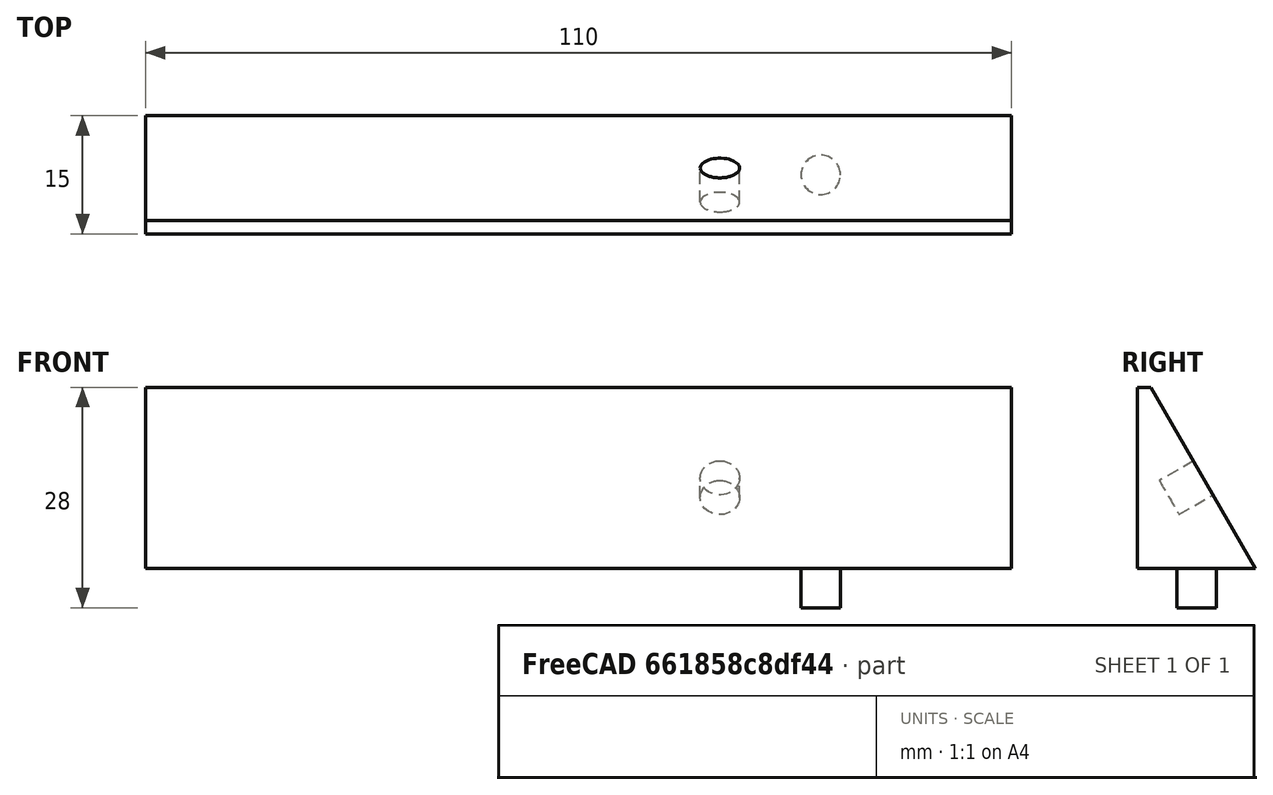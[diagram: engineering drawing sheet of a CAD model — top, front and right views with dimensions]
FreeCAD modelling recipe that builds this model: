
FCSTD DOCUMENT  (FreeCAD 1.0R39319 (Git))
Label: part_v3
License: All rights reserved
LicenseURL: https://en.wikipedia.org/wiki/All_rights_reserved
objects: TechDraw::DrawViewDimension×7, TechDraw::DrawProjGroupItem×4, Sketcher::SketchObject×3, PartDesign::Pad×2, PartDesign::Pocket×1, PartDesign::Body×1, App::DocumentObjectGroup×1, TechDraw::DrawSVGTemplate×1, TechDraw::DrawProjGroup×1, TechDraw::DrawViewImage×1, TechDraw::DrawPage×1
note: 25 computed .brp shape members not serialized (recipe doc carries the construction recipe); baked Part::Feature solids carry a one-line shape summary decoded from their .brp

FEATURE [Sketcher::SketchObject] Sketch  label="Profil"
  ArcFitTolerance = 1e-06
  AttachmentSupport = -> [YZ_Plane]
  FullyConstrained = true
  MakeInternals = false
  MapMode = 5
  Placement = pos=(0,0,0) rot=(0.57735,0.57735,0.57735;2.0944rad)
  sketch-geometry (4):
    g0: LineSegment StartX=0 StartY=0 StartZ=0 EndX=-13.2791 EndY=23 EndZ=0
    g1: LineSegment StartX=-13.2791 StartY=23 StartZ=0 EndX=-15 EndY=23 EndZ=0
    g2: LineSegment StartX=-15 StartY=23 StartZ=0 EndX=-15 EndY=0 EndZ=0
    g3: LineSegment StartX=-15 StartY=0 StartZ=0 EndX=0 EndY=0 EndZ=0
  constraints (12):
    c: Coincident(g-1,g0)
    c: Coincident(g0,g1)
    c: Horizontal(g1)
    c: Coincident(g1,g2)
    c: PointOnObject(g2,g-1)
    c: Vertical(g2)
    c: Coincident(g2,g3)
    c: Coincident(g3,g0)
    c: Angle(g0,g3) = 1.0472
    c: Distance(g3) = 15  'Base'
    c: DistanceY(g0,g0) = 23  'Hauteur'
    c: Distance(g0) = 26.5581  'Face2'
FEATURE [PartDesign::Pad] Pad  label="Corps"
  Direction = (1,0,0)
  Length = 110
  Length2 = 10
  Midplane = true
  Placement = pos=(0,0,0) rot=(1,1,1;2.0944rad)
  Profile = -> Sketch
  ReferenceAxis = -> Sketch [N_Axis]
  Refine = true
  Suppressed = false
  Type = 0
FEATURE [Sketcher::SketchObject] Sketch001  label="ProfilPicot"
  ArcFitTolerance = 1e-06
  AttachmentSupport = -> [XY_Plane]
  FullyConstrained = false
  MakeInternals = false
  MapMode = 5
  expr: .Constraints.MagicAngle = acos(1 / 3)
  expr: Constraints[12] = <<Profil>>.Constraints.Base
  expr: Constraints[18] = <<Profil>>.Constraints.Hauteur
  expr: Constraints[20] = <<Profil>>.Constraints.Base
  expr: Constraints[7] = <<Profil>>.Constraints.Base
  sketch-geometry (11):
    g0: LineSegment [constr] StartX=0 StartY=0 StartZ=0 EndX=5.3033 EndY=-15 EndZ=0
    g1: LineSegment [constr] StartX=5.3033 StartY=-15 StartZ=0 EndX=21.2132 EndY=-15 EndZ=0
    g2: LineSegment [constr] StartX=21.2132 StartY=-15 StartZ=0 EndX=15.9099 EndY=0 EndZ=0
    g3: LineSegment [constr] StartX=15.9099 StartY=0 StartZ=0 EndX=0 EndY=0 EndZ=0
    g4: LineSegment [constr] StartX=15.9099 StartY=0 StartZ=0 EndX=1.76777 EndY=-5 EndZ=0
    g5: LineSegment [constr] StartX=40.3051 StartY=0 StartZ=0 EndX=45.6084 EndY=-15 EndZ=0
    g6: LineSegment [constr] StartX=46.7775 StartY=-18.3068 StartZ=0 EndX=25.0929 EndY=-25.9735 EndZ=0
    g7: LineSegment [constr] StartX=15.9099 StartY=0 StartZ=0 EndX=45.6084 EndY=-15 EndZ=0
    g8: LineSegment [constr] StartX=40.3051 StartY=0 StartZ=0 EndX=21.2132 EndY=-15 EndZ=0
    g9: Circle CenterX=30.7591 CenterY=-7.5 CenterZ=0 NormalX=0 NormalY=0 NormalZ=1 AngleXU=0 Radius=2.5
    g10: LineSegment [constr] StartX=21.2132 StartY=-15 StartZ=0 EndX=0 EndY=-15 EndZ=0
  constraints (32):
    c: Coincident(g-1,g0)
    c: Coincident(g0,g1)
    c: Horizontal(g1)
    c: Coincident(g1,g2)
    c: PointOnObject(g2,g-1)
    c: Coincident(g2,g3)
    c: Coincident(g3,g0)
    c: DistanceY(g0,g0) = 15
    c: Equal(g0,g2)
    c: Coincident(g4,g2)
    c: PointOnObject(g4,g0)
    c: Perpendicular(g2,g4)
    c: Distance(g4) = 15
    c: Angle(g0,g3) = 1.23096  'MagicAngle'
    c: PointOnObject(g5,g-1)
    c: Parallel(g2,g5)
    c: PointOnObject(g6,g5)
    c: Perpendicular(g5,g6)
    c: Distance(g6) = 23
    c: PointOnObject(g6,g2)
    c: DistanceY(g5,g5) = 15
    c: Coincident(g7,g2)
    c: Coincident(g7,g5)
    c: Coincident(g8,g5)
    c: Coincident(g8,g1)
    c: Symmetric(g7,g7,g9)
    c: Diameter(g9) = 5
    c: Coincident(g10,g1)
    c: PointOnObject(g10,g-2)
    c: Horizontal(g10)
    c: DistanceX(g10,g10) = 21.2132  'PointA'
    c: Distance(g2,g0) = 18.3712  'halfCubeHeight'
FEATURE [PartDesign::Pad] Pad001  label="Picot"
  BaseFeature = -> Pad
  Direction = (0,0,1)
  Length = 5
  Length2 = 10
  Placement = pos=(0,0,0) rot=(1,1,1;2.0944rad)
  Profile = -> Sketch001
  ReferenceAxis = -> Sketch001 [N_Axis]
  Refine = true
  Reversed = true
  Suppressed = false
  Type = 0
FEATURE [Sketcher::SketchObject] Sketch002  label="ProfilTrou"
  ArcFitTolerance = 1e-06
  AttachmentSupport = -> [Pad001]
  FullyConstrained = false
  MakeInternals = false
  MapMode = 5
  Placement = pos=(0,1e-16,1e-16) rot=(-0.447214,-0.447214,-0.774597;1.82348rad)
  expr: Constraints[11] = <<Profil>>.Constraints.Base
  expr: Constraints[18] = acos(1 / 3)
  expr: Constraints[19] = <<Profil>>.Constraints.Face2
  expr: Constraints[7] = <<ProfilPicot>>.Constraints.PointA
  sketch-geometry (8):
    g0: LineSegment [constr] StartX=0 StartY=21.2132 StartZ=0 EndX=0 EndY=5.3033 EndZ=0
    g1: LineSegment [constr] StartX=0 StartY=5.3033 StartZ=0 EndX=26.5581 EndY=14.693 EndZ=0
    g2: LineSegment [constr] StartX=26.5581 StartY=30.6029 StartZ=0 EndX=0 EndY=21.2132 EndZ=0
    g3: LineSegment [constr] StartX=0 StartY=0 StartZ=0 EndX=0 EndY=21.2132 EndZ=0
    g4: LineSegment [constr] StartX=30.1461 StartY=31.8715 StartZ=0 EndX=35.1461 EndY=17.7293 EndZ=0
    g5: LineSegment [constr] StartX=0 StartY=21.2132 StartZ=0 EndX=26.5581 EndY=14.693 EndZ=0
    g6: LineSegment [constr] StartX=26.5581 StartY=30.6029 StartZ=0 EndX=0 EndY=5.3033 EndZ=0
    g7: Circle CenterX=13.2791 CenterY=17.9531 CenterZ=0 NormalX=0 NormalY=0 NormalZ=1 AngleXU=0 Radius=2.5
  constraints (21):
    c: PointOnObject(g0,g-2)
    c: Vertical(g0)
    c: Coincident(g0,g1)
    c: Coincident(g2,g0)
    c: Parallel(g2,g1)
    c: Coincident(g3,g-1)
    c: Coincident(g3,g0)
    c: DistanceY(g3,g3) = 21.2132
    c: PointOnObject(g4,g2)
    c: PointOnObject(g4,g1)
    c: Perpendicular(g2,g4)
    c: Distance(g4) = 15
    c: Coincident(g2,g6)
    c: PointOnObject(g7,g5)
    c: PointOnObject(g7,g6)
    c: Coincident(g2,g5)
    c: Coincident(g6,g0)
    c: Coincident(g1,g5)
    c: Angle(g1,g0) = 1.23096
    c: DistanceX(g2,g2) = 26.5581
    c: Equal(g2,g1)
FEATURE [PartDesign::Pocket] Pocket
  BaseFeature = -> Pad001
  Direction = (-2e-16,-0.866025,-0.5)
  Length = 5
  Length2 = 5
  Placement = pos=(0,0,0) rot=(1,1,1;2.0944rad)
  Profile = -> Sketch002
  ReferenceAxis = -> Sketch002 [N_Axis]
  Refine = true
  Suppressed = false
  Type = 0
FEATURE [PartDesign::Body] Body
  AllowCompound = false
  Group = -> [Sketch,Pad,Sketch001,Pad001,Sketch002,Pocket]
  Origin = -> Origin
  Placement = pos=(0,15,0) rot=(0,0,1;0rad)
  Tip = -> Pocket
FEATURE [App::DocumentObjectGroup] Group
  Group = -> [Body]
FEATURE [TechDraw::DrawSVGTemplate] Template
  EditableTexts = approval_person=B. Hecate; creator=A. Nemesis; date_of_issue=03/10/2025; document_type=Component Drawing; general_tolerances=ISO 2768-m; identification_number=DN; language_code=EN; part_material=Stainless steel Mat.No. 1.4301; revision_index=AAA; scale=1 : 1; sheet_number=1 / 1; title=part_v3
  Height = 210
  Orientation = 1
  Template = <userpath>/AppData/Local/Programs/FreeCAD 1.0/data/Mod/TechDraw/Templates/A4_Landscape_ISO5457_minimal.svg
  Width = 297
FEATURE [TechDraw::DrawProjGroupItem] View  label="Front"
  CoarseView = false
  Direction = (0,-1,0)
  Focus = 100
  HardHidden = true
  IsoCount = 0
  IsoHidden = false
  IsoVisible = false
  LockPosition = true
  Perspective = false
  Rotation = 0
  RotationVector = (1,0,0)
  ScaleType = 2
  ScrubCount = 1
  SeamHidden = false
  SeamVisible = false
  SmoothHidden = true
  SmoothVisible = true
  Source = -> [Pocket]
  Type = 0
  X = 0
  XDirection = (1,0,0)
  Y = 0
FEATURE [TechDraw::DrawProjGroupItem] ProjItem  label="Bottom"
  CoarseView = false
  Direction = (0,0,-1)
  Focus = 100
  HardHidden = true
  IsoCount = 0
  IsoHidden = false
  IsoVisible = false
  LockPosition = false
  Perspective = false
  Rotation = 0
  RotationVector = (1,0,0)
  ScaleType = 0
  ScrubCount = 1
  SeamHidden = false
  SeamVisible = false
  SmoothHidden = false
  SmoothVisible = true
  Source = -> [Pocket]
  Type = 5
  X = 0
  XDirection = (1,0,0)
  Y = -37.0918
FEATURE [TechDraw::DrawProjGroupItem] ProjItem001  label="Left"
  CoarseView = false
  Direction = (-1,-1e-16,0)
  Focus = 100
  HardHidden = true
  IsoCount = 0
  IsoHidden = false
  IsoVisible = false
  LockPosition = false
  Perspective = false
  Rotation = 0
  RotationVector = (1,0,0)
  ScaleType = 0
  ScrubCount = 1
  SeamHidden = false
  SeamVisible = false
  SmoothHidden = false
  SmoothVisible = true
  Source = -> [Pocket]
  Type = 1
  X = 82.4659
  XDirection = (1e-16,-1,0)
  Y = 0
FEATURE [TechDraw::DrawProjGroupItem] ProjItem002  label="Top"
  CoarseView = false
  Direction = (0,0,1)
  Focus = 100
  HardHidden = true
  IsoCount = 0
  IsoHidden = false
  IsoVisible = false
  LockPosition = false
  Perspective = false
  Rotation = 0
  RotationVector = (1,0,0)
  ScaleType = 0
  ScrubCount = 1
  SeamHidden = false
  SeamVisible = false
  SmoothHidden = false
  SmoothVisible = true
  Source = -> [Pocket]
  Type = 4
  X = 0
  XDirection = (1,0,0)
  Y = 41.9572
FEATURE [TechDraw::DrawProjGroup] ProjGroup
  Anchor = -> View
  AutoDistribute = false
  LockPosition = false
  ProjectionType = 0
  Rotation = 0
  ScaleType = 0
  Source = -> [Pocket]
  Views = -> [View,ProjItem,ProjItem001,ProjItem002]
  X = 99.9457
  Y = 131.652
  spacingX = 15
  spacingY = 15
FEATURE [TechDraw::DrawViewDimension] Dimension
  AngleOverride = false
  Arbitrary = false
  ArbitraryTolerances = false
  BoxCorners = (2) [(-55,-14,-1e-07),(55,14,1e-07)]
  EqualTolerance = true
  ExtensionAngle = 0
  FormatSpec = %.2w
  FormatSpecOverTolerance = %+.2w
  FormatSpecUnderTolerance = %+.2w
  Inverted = false
  LineAngle = 0
  LockPosition = false
  MeasureType = 1
  OverTolerance = 0
  References2D = -> [View]
  Rotation = 0
  ScaleType = 0
  TheoreticalExact = false
  Type = 2
  UnderTolerance = 0
  X = -83.2169
  Y = 2.5
FEATURE [TechDraw::DrawViewDimension] Dimension001
  AngleOverride = false
  Arbitrary = false
  ArbitraryTolerances = false
  BoxCorners = (2) [(-55,-7.5,0),(55,7.5,0)]
  EqualTolerance = true
  ExtensionAngle = 0
  FormatSpec = %.2w
  FormatSpecOverTolerance = %+.2w
  FormatSpecUnderTolerance = %+.2w
  Inverted = false
  LineAngle = 0
  LockPosition = false
  MeasureType = 1
  OverTolerance = 0
  References2D = -> [ProjItem]
  Rotation = 0
  ScaleType = 0
  TheoreticalExact = false
  Type = 1
  UnderTolerance = 0
  X = -13.091
  Y = -24.3834
FEATURE [TechDraw::DrawViewDimension] Dimension002
  AngleOverride = false
  Arbitrary = false
  ArbitraryTolerances = false
  BoxCorners = (2) [(-55,-7.5,0),(55,7.5,0)]
  EqualTolerance = true
  ExtensionAngle = 0
  FormatSpec = %.2w
  FormatSpecOverTolerance = %+.2w
  FormatSpecUnderTolerance = %+.2w
  Inverted = false
  LineAngle = 0
  LockPosition = false
  MeasureType = 1
  OverTolerance = 0
  References2D = -> [ProjItem]
  Rotation = 0
  ScaleType = 0
  TheoreticalExact = false
  Type = 2
  UnderTolerance = 0
  X = -83.0266
  Y = 0
FEATURE [TechDraw::DrawViewDimension] Dimension003
  AngleOverride = false
  Arbitrary = false
  ArbitraryTolerances = false
  BoxCorners = (2) [(-7.5,-14,-1e-07),(7.5,14,1e-07)]
  EqualTolerance = true
  ExtensionAngle = 0
  FormatSpec = %.2w
  FormatSpecOverTolerance = %+.2w
  FormatSpecUnderTolerance = %+.2w
  Inverted = false
  LineAngle = 0
  LockPosition = false
  MeasureType = 1
  OverTolerance = 0
  References2D = -> [ProjItem001]
  Rotation = 0
  ScaleType = 0
  TheoreticalExact = false
  Type = 0
  UnderTolerance = 0
  X = 6.63953
  Y = 39.5286
FEATURE [TechDraw::DrawViewDimension] Dimension004
  AngleOverride = false
  Arbitrary = false
  ArbitraryTolerances = false
  BoxCorners = (2) [(-55,-7.5,0),(55,7.5,0)]
  EqualTolerance = true
  ExtensionAngle = 0
  FormatSpec = ⌀%.2w
  FormatSpecOverTolerance = %+.2w
  FormatSpecUnderTolerance = %+.2w
  Inverted = false
  LineAngle = 0
  LockPosition = false
  MeasureType = 1
  OverTolerance = 0
  References2D = -> [ProjItem]
  Rotation = 0
  ScaleType = 0
  TheoreticalExact = false
  Type = 5
  UnderTolerance = 0
  X = 16.1373
  Y = 20.8992
FEATURE [TechDraw::DrawViewImage] ActiveView
  Height = 102.4
  ImageFile = <userpath>/AppData/Local/cache/FreeCAD/Cache/FreeCAD_Doc_03f074d4-d428-461f-952a-9dc7c3b047c4_f18cbb_379585/Pag4186.tmp.png
  LockPosition = false
  Rotation = 0
  ScaleType = 2
  Width = 128
  X = 253.79
  Y = 162.142
FEATURE [TechDraw::DrawViewDimension] Dimension005
  AngleOverride = false
  Arbitrary = false
  ArbitraryTolerances = false
  BoxCorners = (2) [(-55,-7.5,0),(55,7.5,0)]
  EqualTolerance = true
  ExtensionAngle = 0
  FormatSpec = %.2w
  FormatSpecOverTolerance = %+.2w
  FormatSpecUnderTolerance = %+.2w
  Inverted = false
  LineAngle = 0
  LockPosition = false
  MeasureType = 1
  OverTolerance = 0
  References2D = -> [ProjItem002]
  Rotation = 0
  ScaleType = 0
  TheoreticalExact = false
  Type = 1
  UnderTolerance = 0
  X = 36.4766
  Y = 23.8033
FEATURE [TechDraw::DrawViewDimension] Dimension006
  AngleOverride = false
  Arbitrary = false
  ArbitraryTolerances = false
  BoxCorners = (2) [(-55,-7.5,0),(55,7.5,0)]
  EqualTolerance = true
  ExtensionAngle = 0
  FormatSpec = %.2w
  FormatSpecOverTolerance = %+.2w
  FormatSpecUnderTolerance = %+.2w
  Inverted = false
  LineAngle = 0
  LockPosition = false
  MeasureType = 1
  OverTolerance = 0
  References2D = -> [ProjItem]
  Rotation = 0
  ScaleType = 0
  TheoreticalExact = false
  Type = 1
  UnderTolerance = 0
  X = 47.6414
  Y = -19.9892
FEATURE [TechDraw::DrawPage] Page
  KeepUpdated = true
  NextBalloonIndex = 1
  ProjectionType = 0
  Template = -> Template
  Views = -> [ProjGroup,Dimension,Dimension001,Dimension002,Dimension003,Dimension004,ActiveView,Dimension005,Dimension006]
